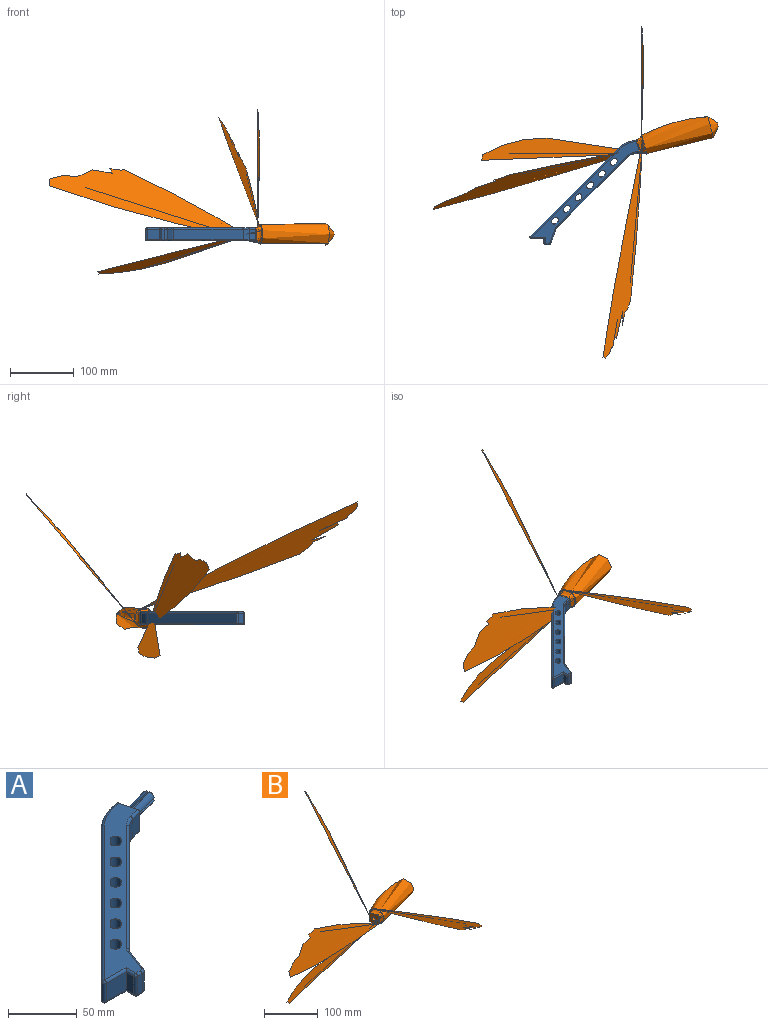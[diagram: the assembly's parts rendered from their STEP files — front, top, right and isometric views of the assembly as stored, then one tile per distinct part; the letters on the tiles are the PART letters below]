
ASSEMBLY  parts=2 mates=1
PART A: 102 faces, bbox 199x167.6x20 mm
  f0: plane 20x19.32mm, normal (0.97,0.26,0), area 333.8mm2, adj f1,f2,f5,f6,f41,f44,f55,f58
  f1: plane 168.84x160.43mm, normal (0,0,1), area 3071.6mm2, adj f0,f17,f18,f19,f20,f21,f22,f23
  f2: plane 168.84x160.43mm, normal (0,0,-1), area 3071.6mm2, adj f0,f17,f18,f19,f20,f21,f22,f23
  f3: plane 109.43x109.43mm, normal (0.71,-0.71,0), area 2476.1mm2, adj f4,f13,f43,f57
  f4: cylinder r=20mm len=16mm, axis (0,0,-1), area 167.6mm2, adj f3,f5,f42,f56
  f5: plane 16x9.66mm, normal (0.26,-0.97,0), area 160mm2, adj f0,f4,f41,f55
  f6: plane 16x9.66mm, normal (-0.26,0.97,0), area 160mm2, adj f0,f7,f44,f58
  f7: cylinder r=40mm len=17.93mm, axis (0,0,-1), area 335.1mm2, adj f6,f8,f46,f60
  f8: plane 138.01x138.01mm, normal (-0.71,0.71,0), area 3122.7mm2, adj f7,f14,f48,f62
  f9: plane 20.17x16mm, normal (0,-1,0), area 322.7mm2, adj f10,f14,f52,f66
  f10: plane 16x8mm, normal (-1,0,0), area 128mm2, adj f9,f15,f54,f68
  f11: plane 16x4.5mm, normal (0,-1,0), area 72mm2, adj f15,f16,f51,f65
  f12: plane 20.91x16mm, normal (0.94,-0.34,0), area 356mm2, adj f13,f16,f47,f61
  f13: cylinder r=10mm len=16mm, axis (0,0,1), area 69.8mm2, adj f3,f12,f45,f59
  f14: cylinder r=2mm len=16mm, axis (0,0,-1), area 75.4mm2, adj f8,f9,f50,f64
  f15: cylinder r=2mm len=16mm, axis (0,0,-1), area 50.3mm2, adj f10,f11,f53,f67
  f16: cylinder r=5mm len=16mm, axis (0,0,-1), area 97.7mm2, adj f11,f12,f49,f63
  f17: cylinder r=4mm len=20mm, axis (0,0,1), area 251.3mm2, adj f1,f2,f18,f20
  f18: plane 20x2.83mm, normal (-0.71,0.71,0), area 80mm2, adj f1,f2,f17,f19
  f19: cylinder r=4mm len=20mm, axis (0,0,1), area 251.3mm2, adj f1,f2,f18,f20
  f20: plane 20x2.83mm, normal (0.71,-0.71,0), area 80mm2, adj f1,f2,f17,f19
  f21: cylinder r=4mm len=20mm, axis (0,0,1), area 251.3mm2, adj f1,f2,f22,f24
  f22: plane 20x2.83mm, normal (-0.71,0.71,0), area 80mm2, adj f1,f2,f21,f23
  f23: cylinder r=4mm len=20mm, axis (0,0,1), area 251.3mm2, adj f1,f2,f22,f24
  f24: plane 20x2.83mm, normal (0.71,-0.71,0), area 80mm2, adj f1,f2,f21,f23
  f25: cylinder r=4mm len=20mm, axis (0,0,1), area 251.3mm2, adj f1,f2,f26,f28
  f26: plane 20x2.83mm, normal (-0.71,0.71,0), area 80mm2, adj f1,f2,f25,f27
  f27: cylinder r=4mm len=20mm, axis (0,0,1), area 251.3mm2, adj f1,f2,f26,f28
  f28: plane 20x2.83mm, normal (0.71,-0.71,0), area 80mm2, adj f1,f2,f25,f27
  f29: cylinder r=4mm len=20mm, axis (0,0,1), area 251.3mm2, adj f1,f2,f30,f32
  f30: plane 20x2.83mm, normal (-0.71,0.71,0), area 80mm2, adj f1,f2,f29,f31
  f31: cylinder r=4mm len=20mm, axis (0,0,1), area 251.3mm2, adj f1,f2,f30,f32
  f32: plane 20x2.83mm, normal (0.71,-0.71,0), area 80mm2, adj f1,f2,f29,f31
  f33: cylinder r=4mm len=20mm, axis (0,0,1), area 251.3mm2, adj f1,f2,f34,f36
  f34: plane 20x2.83mm, normal (-0.71,0.71,0), area 80mm2, adj f1,f2,f33,f35
  f35: cylinder r=4mm len=20mm, axis (0,0,1), area 251.3mm2, adj f1,f2,f34,f36
  f36: plane 20x2.83mm, normal (0.71,-0.71,0), area 80mm2, adj f1,f2,f33,f35
  f37: cylinder r=4mm len=20mm, axis (0,0,1), area 251.3mm2, adj f1,f2,f38,f40
  f38: plane 20x2.83mm, normal (-0.71,0.71,0), area 80mm2, adj f1,f2,f37,f39
  f39: cylinder r=4mm len=20mm, axis (0,0,1), area 251.3mm2, adj f1,f2,f38,f40
  f40: plane 20x2.83mm, normal (0.71,-0.71,0), area 80mm2, adj f1,f2,f37,f39
  f41: cylinder r=2mm len=10.18mm, axis (0.97,0.26,0), area 31.4mm2, adj f0,f2,f5,f42
  f42: torus R=22mm, axis (0,0,1), area 34.1mm2, adj f2,f4,f41,f43
  f43: cylinder r=2mm len=110.84mm, axis (0.71,0.71,0), area 486.2mm2, adj f2,f3,f42,f45
  f44: cylinder r=2mm len=10.18mm, axis (-0.97,-0.26,0), area 31.4mm2, adj f0,f2,f6,f46
  f45: torus R=12mm, axis (0,0,1), area 14.7mm2, adj f2,f13,f43,f47
  f46: torus R=38mm, axis (0,0,1), area 64.6mm2, adj f2,f7,f44,f48
  f47: cylinder r=2mm len=21.59mm, axis (0.34,0.94,0), area 69.9mm2, adj f2,f12,f45,f49
  f48: cylinder r=2mm len=139.42mm, axis (-0.71,-0.71,0), area 613.1mm2, adj f2,f8,f46,f50
  f49: torus R=3mm, axis (0,0,1), area 16.4mm2, adj f2,f16,f47,f51
  f50: sphere r=2mm, area 9.4mm2, adj f14,f48,f52
  f51: cylinder r=2mm len=4.5mm, axis (1,0,0), area 14.1mm2, adj f2,f11,f49,f53
  f52: cylinder r=2mm len=22.17mm, axis (1,0,0), area 65.7mm2, adj f2,f9,f50,f54
  f53: sphere r=2mm, area 6.3mm2, adj f15,f51,f54
  f54: cylinder r=2mm len=10mm, axis (0,-1,0), area 27.4mm2, adj f2,f10,f52,f53
  f55: cylinder r=2mm len=10.18mm, axis (-0.97,-0.26,0), area 31.4mm2, adj f0,f1,f5,f56
  f56: torus R=22mm, axis (0,0,1), area 34.1mm2, adj f1,f4,f55,f57
  f57: cylinder r=2mm len=110.84mm, axis (-0.71,-0.71,0), area 486.2mm2, adj f1,f3,f56,f59
  f58: cylinder r=2mm len=10.18mm, axis (0.97,0.26,0), area 31.4mm2, adj f0,f1,f6,f60
  f59: torus R=12mm, axis (0,0,1), area 14.7mm2, adj f1,f13,f57,f61
  f60: torus R=38mm, axis (0,0,1), area 64.6mm2, adj f1,f7,f58,f62
  f61: cylinder r=2mm len=21.59mm, axis (-0.34,-0.94,0), area 69.9mm2, adj f1,f12,f59,f63
  f62: cylinder r=2mm len=139.42mm, axis (0.71,0.71,0), area 613.1mm2, adj f1,f8,f60,f64
  f63: torus R=3mm, axis (0,0,1), area 16.4mm2, adj f1,f16,f61,f65
  f64: sphere r=2mm, area 9.4mm2, adj f14,f62,f66
  f65: cylinder r=2mm len=4.5mm, axis (-1,0,0), area 14.1mm2, adj f1,f11,f63,f67
  f66: cylinder r=2mm len=22.17mm, axis (-1,0,0), area 65.7mm2, adj f1,f9,f64,f68
  f67: sphere r=2mm, area 6.3mm2, adj f15,f65,f68
  f68: cylinder r=2mm len=10mm, axis (0,1,0), area 27.4mm2, adj f1,f10,f66,f67
  f69: plane 28.78x7.71mm, normal (-0.26,0.97,0), area 56.6mm2, adj f0,f70,f84,f94
  f70: cylinder r=5mm len=29.79mm, axis (-0.97,-0.26,0), area 174mm2, adj f0,f69,f71,f92
  f71: plane 29.28x9.55mm, normal (0,0,-1), area 56.6mm2, adj f0,f70,f72,f90
  f72: plane 28.78x7.71mm, normal (0.26,-0.97,0), area 59.6mm2, adj f0,f71,f73,f88
  f73: plane 29.28x9.55mm, normal (0,0,1), area 56.6mm2, adj f0,f72,f74,f86
  f74: cylinder r=5mm len=29.79mm, axis (-0.97,-0.26,0), area 174mm2, adj f0,f73,f75,f87
  f75: plane 28.78x7.71mm, normal (-0.26,0.97,0), area 56.6mm2, adj f0,f74,f76,f89
  f76: plane 29.3x9.64mm, normal (0,0,-1), area 59.6mm2, adj f0,f75,f77,f91
  f77: plane 28.78x7.71mm, normal (0.26,-0.97,0), area 56.6mm2, adj f0,f76,f78,f93
  f78: cylinder r=5mm len=29.79mm, axis (-0.97,-0.26,0), area 174mm2, adj f0,f77,f79,f95
  f79: plane 29.28x9.55mm, normal (0,0,1), area 56.6mm2, adj f0,f78,f80,f97
  f80: plane 28.78x7.71mm, normal (-0.26,0.97,0), area 59.6mm2, adj f0,f79,f81,f99
  f81: plane 29.28x9.55mm, normal (0,0,-1), area 56.6mm2, adj f0,f80,f82,f101
  f82: cylinder r=5mm len=29.79mm, axis (-0.97,-0.26,0), area 174mm2, adj f0,f81,f83,f100
  f83: plane 28.78x7.71mm, normal (0.26,-0.97,0), area 56.6mm2, adj f0,f82,f84,f98
  f84: plane 29.3x9.64mm, normal (0,0,1), area 59.6mm2, adj f0,f69,f83,f96
  f85: plane 9.3x8.98mm, normal (0.97,0.26,0), area 53.7mm2, adj f86,f87,f88,f89,f90,f91,f92,f93
  f86: plane 2.08x0.62mm, normal (0.68,0.18,0.71), area 0.5mm2, adj f73,f85,f87,f88
  f87: cone r=4.8mm half-angle=45deg, axis (-0.97,-0.26,0), area 1.5mm2, adj f74,f85,f86,f89
  f88: plane 2.4x0.25mm, normal (0.87,-0.5,0), area 0.6mm2, adj f72,f85,f86,f90
  f89: plane 2.1x0.25mm, normal (0.5,0.87,0), area 0.5mm2, adj f75,f85,f87,f91
  f90: plane 2.08x0.62mm, normal (0.68,0.18,-0.71), area 0.5mm2, adj f71,f85,f88,f92
  f91: plane 2.32x0.76mm, normal (0.68,0.18,-0.71), area 0.6mm2, adj f76,f85,f89,f93
  f92: cone r=4.8mm half-angle=45deg, axis (-0.97,-0.26,0), area 1.5mm2, adj f70,f85,f90,f94
  f93: plane 2.1x0.25mm, normal (0.87,-0.5,0), area 0.5mm2, adj f77,f85,f91,f95
  f94: plane 2.1x0.25mm, normal (0.5,0.87,0), area 0.5mm2, adj f69,f85,f92,f96
  f95: cone r=4.8mm half-angle=45deg, axis (-0.97,-0.26,0), area 1.5mm2, adj f78,f85,f93,f97
  f96: plane 2.32x0.76mm, normal (0.68,0.18,0.71), area 0.6mm2, adj f84,f85,f94,f98
  f97: plane 1.98x0.74mm, normal (0.68,0.18,0.71), area 0.5mm2, adj f79,f85,f95,f99
  f98: plane 2.1x0.25mm, normal (0.87,-0.5,0), area 0.5mm2, adj f83,f85,f96,f100
  f99: plane 2.4x0.25mm, normal (0.5,0.87,0), area 0.6mm2, adj f80,f85,f97,f101
  f100: cone r=4.8mm half-angle=45deg, axis (-0.97,-0.26,0), area 1.5mm2, adj f82,f85,f98,f101
  f101: plane 1.98x0.74mm, normal (0.68,0.18,-0.71), area 0.5mm2, adj f81,f85,f99,f100
PART B: 45 faces, bbox 24436.3x31111.9x20512.6 mm
  f0: plane 6.13x5.92mm, normal (0.97,0.26,0), area 29.5mm2, adj f2
  f1: revolved ~112.6x60.5mm, area 309152988.1mm2, adj f2,f37,f38,f39,f40,f41,f42,f43
  f2: torus R=3.06mm, axis (-0.97,-0.26,0), area 1526.2mm2, adj f0,f1
  f3: plane 16.01x1.62mm, normal (-0.26,0.97,0), area 17.5mm2, adj f7,f25,f28,f34
  f4: plane 15.89x5.76mm, normal (0,0,-1), area 17.5mm2, adj f7,f25,f26,f30
  f5: plane 16.01x1.62mm, normal (0.26,-0.97,0), area 17.5mm2, adj f7,f26,f27,f31
  f6: plane 15.89x5.76mm, normal (0,0,1), area 17.5mm2, adj f7,f27,f28,f35
  f7: plane 20x19.32mm, normal (-0.97,-0.26,0), area 332.1mm2, adj f3,f4,f5,f6,f9,f10,f11,f12
  f8: plane 9.96x9.62mm, normal (-0.97,-0.26,0), area 64.5mm2, adj f9,f10,f11,f12,f13,f14,f15,f16
  f9: plane 31.4x10.1mm, normal (0,0,1), area 60.2mm2, adj f7,f8,f10,f24
  f10: plane 30.91x8.28mm, normal (0.26,-0.97,0), area 70.4mm2, adj f7,f8,f9,f11
  f11: plane 31.4x10.1mm, normal (0,0,-1), area 60.2mm2, adj f7,f8,f10,f12
  f12: cylinder r=5.1mm len=31.91mm, axis (-0.97,-0.26,0), area 185.4mm2, adj f7,f8,f11,f13
  f13: plane 30.91x8.28mm, normal (-0.26,0.97,0), area 60.2mm2, adj f7,f8,f12,f14
  f14: plane 31.48x10.41mm, normal (0,0,1), area 70.4mm2, adj f7,f8,f13,f15
  f15: plane 30.91x8.28mm, normal (0.26,-0.97,0), area 60.2mm2, adj f7,f8,f14,f16
  f16: cylinder r=5.1mm len=31.91mm, axis (-0.97,-0.26,0), area 185.4mm2, adj f7,f8,f15,f17
  f17: plane 31.4x10.1mm, normal (0,0,-1), area 60.2mm2, adj f7,f8,f16,f18
  f18: plane 30.91x8.28mm, normal (-0.26,0.97,0), area 70.4mm2, adj f7,f8,f17,f19
  f19: plane 31.4x10.1mm, normal (0,0,1), area 60.2mm2, adj f7,f8,f18,f20
  f20: cylinder r=5.1mm len=31.91mm, axis (-0.97,-0.26,0), area 185.4mm2, adj f7,f8,f19,f21
  f21: plane 30.91x8.28mm, normal (0.26,-0.97,0), area 60.2mm2, adj f7,f8,f20,f22
  f22: plane 31.48x10.41mm, normal (0,0,-1), area 70.4mm2, adj f7,f8,f21,f23
  f23: plane 30.91x8.28mm, normal (-0.26,0.97,0), area 60.2mm2, adj f7,f8,f22,f24
  f24: cylinder r=5.1mm len=31.91mm, axis (-0.97,-0.26,0), area 185.4mm2, adj f7,f8,f9,f23
  f25: cylinder r=2mm len=3.59mm, axis (-0.97,-0.26,0), area 8.3mm2, adj f3,f4,f7,f32
  f26: cylinder r=2mm len=3.59mm, axis (0.97,0.26,0), area 8.3mm2, adj f4,f5,f7,f29
  f27: cylinder r=2mm len=3.59mm, axis (-0.97,-0.26,0), area 8.3mm2, adj f5,f6,f7,f33
  f28: cylinder r=2mm len=3.59mm, axis (0.97,0.26,0), area 8.3mm2, adj f3,f6,f7,f36
  f29: bspline ~10.58x10.49mm, area 54.5mm2, adj f26,f30,f31,f42
  f30: bspline ~16.91x11.82mm, area 143.1mm2, adj f4,f29,f32,f40
  f31: bspline ~17.55x10.41mm, area 143.1mm2, adj f5,f29,f33,f44
  f32: bspline ~10.86x10.1mm, area 54.5mm2, adj f25,f30,f34,f38
  f33: bspline ~10.86x10.39mm, area 54.5mm2, adj f27,f31,f35,f43
  f34: bspline ~17.55x8.17mm, area 143.1mm2, adj f3,f32,f36,f37
  f35: bspline ~16.99x11.75mm, area 143.1mm2, adj f6,f33,f36,f41
  f36: bspline ~10.49x10.46mm, area 54.5mm2, adj f28,f34,f35,f39
  f37: bspline ~15.48x2.76mm, area 20.3mm2, adj f1,f34,f38,f39
  f38: bspline ~13746.71x12616.34mm, area 8658.1mm2, adj f1,f32,f37,f40
  f39: bspline ~20159.12x16433.59mm, area 92361.2mm2, adj f1,f36,f37,f41
  f40: bspline ~14.99x4.87mm, area 20.3mm2, adj f1,f30,f38,f42
  f41: bspline ~14.99x4.87mm, area 20.3mm2, adj f1,f35,f39,f43
  f42: bspline ~24436.32x15136.94mm, area 126715.4mm2, adj f1,f29,f40,f44
  f43: bspline ~18645.03x12290.58mm, area 64953.5mm2, adj f1,f33,f41,f44
  f44: bspline ~15.48x2.11mm, area 20.3mm2, adj f1,f31,f42,f43
PLACE A t=(-78.58,-46.47,25.8)mm
PLACE B t=(-147.29,-60.49,25.8)mm
MATE fastened B.f2 <-> A.f82  axis (-0.97,-0.26,0) through (90.5,91.01,25.8)mm
